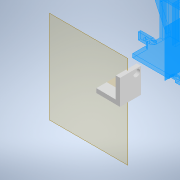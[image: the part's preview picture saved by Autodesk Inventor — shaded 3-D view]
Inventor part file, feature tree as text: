
AUTODESK INVENTOR PART (.ipt)
format: ipt  version: 2020 (Build 240168000, 168)  size: 116,736 bytes
history: native  units: mm
features: hole x2, sketch x2, plane x1, extrude x1
ambient origin geometry x8: Origin, YZ Plane, XZ Plane, XY Plane, X Axis, Y Axis, Z Axis, Center Point
bodies: Solid1 (feature_tree)
feature tree (6):
  plane  "Work Plane1"
  extrude  "Extrusion1"  Depth=50.0mm TaperAngle=0.0deg
  hole  "Hole2"  [1 undecoded]
  sketch  "Sketch1"  dims[d1=10.0mm d2=50.0mm d3=0.0mm]
  sketch  "Sketch2"  dims[d4=6.6mm d5=6.0mm d6=16.0mm d7=8.0mm d8=90.0deg d9=8.0mm d10=0.0mm d11=10.0mm d12=10.0mm d13=60.0mm]
  hole  "Hole1"  [1 undecoded]
note: 2 required parameter values undecoded (feature->parameter linkage not recoverable at this tier; creation-order binding heuristic only, values carry confidence <= 0.55)
